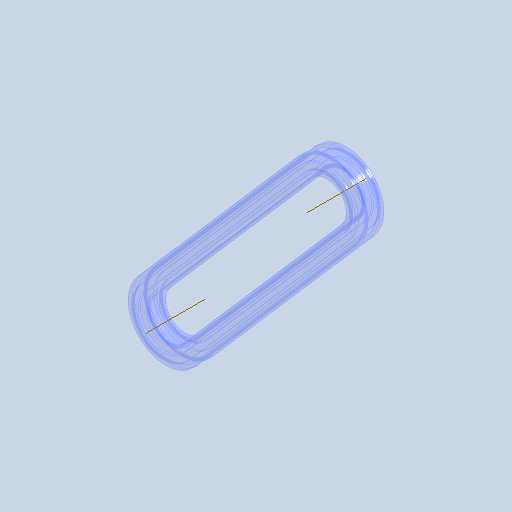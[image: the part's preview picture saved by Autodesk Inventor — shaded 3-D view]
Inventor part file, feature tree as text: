
AUTODESK INVENTOR PART (.ipt)
format: ipt  version: 2022.1 (Build 261234000, 234)  size: 167,424 bytes
history: native  units: mm
features: other x4, plane x2, sweep x1, pattern_linear x1, sketch x1
ambient origin geometry x8: Origin, YZ Plane, XZ Plane, XY Plane, X Axis, Y Axis, Z Axis, Center Point
bodies: Solid1 (feature_tree)
feature tree (9):
  other  "Eje de trabajo1"
  other  "Eje de trabajo2"
  plane  "Plano de trabajo2"
  plane  "Plano de trabajo3"
  other  "Trayectoria"
  other  "Plano de sección"
  sweep  "Sólido"
  pattern_linear  "Strand Pattern"  Spacing1=5.08mm  [1 undecoded]
  sketch  "Boceto de sección"  dims[d2=0.0mm d4=0.0mm d21=5.08mm d22=10.16mm d23=9.65mm d24=3.0mm d28=10.0mm d30=16.59mm d31=14.73mm d32=19.6mm d33=0.0mm d34=0.0mm d35=0.0mm d36=0.0mm d37=0.0mm]
note: 1 required parameter value undecoded (feature->parameter linkage not recoverable at this tier; creation-order binding heuristic only, values carry confidence <= 0.55)
